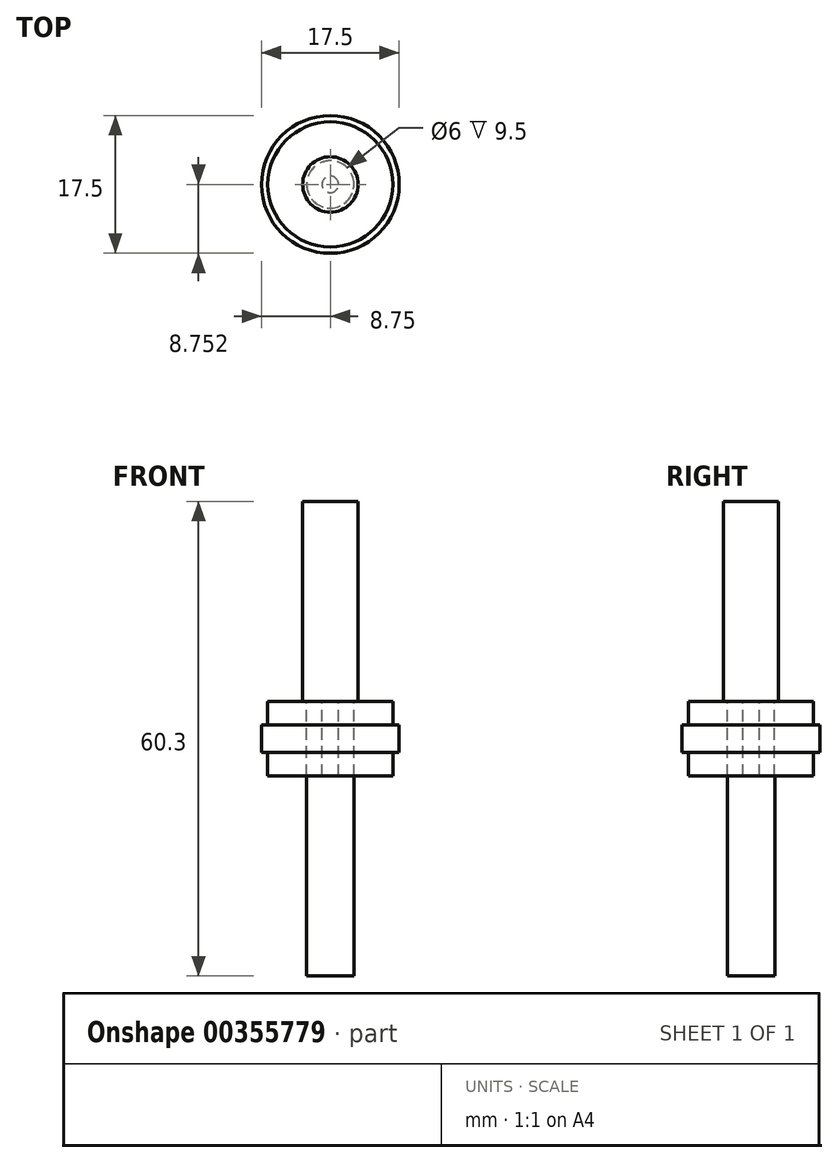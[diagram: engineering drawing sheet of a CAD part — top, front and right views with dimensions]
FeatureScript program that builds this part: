
annotation { "Feature Type Name" : "Feature", "Feature Type Description" : "" }
export const myFeature = defineFeature(function(context is Context, id is Id, definition is map)
    precondition{}
    {
        {
            var Q0;
            Q0=qCreatedBy(makeId("Top.planeOp"),FACE);
            var sketch = newSketch(context, id + "F0", { "sketchPlane" : qUnion([Q0])});
            skCircle(sketch, "E0", {"center": v(-41.02, 34.52) * mm, "radius": 7.95 * mm});
            skSolve(sketch);
        }
        {
            var Q0;
            Q0 = qSketchRegion(id + "F0", true);
            extrude(context, id + "F1", {"entities" : qUnion([Q0]), "depth" : 3 * mm});
        }
        {
            var Q0;
            Q0=makeQuery(id+"F1.opExtrude","CAP_FACE",FACE,{"disambiguationData":[OSD([sQuery(id+"F0.wireOp",EDGE,"E0")])],"isStart":false});
            var sketch = newSketch(context, id + "F2", { "sketchPlane" : qUnion([Q0])});
            skCircle(sketch, "E1", {"center": v(-41.02, 34.52) * mm, "radius": 8.75 * mm});
            skSolve(sketch);
        }
        {
            var Q0;
            Q0 = qSketchRegion(id + "F2", true);
            extrude(context, id + "F3", {"entities" : qUnion([Q0]), "operationType" : NewBodyOperationType.ADD, "depth" : 3.5 * mm});
        }
        {
            var Q0;
            Q0=makeQuery(id+"F3.opExtrude","CAP_FACE",FACE,{"disambiguationData":[OSD([sQuery(id+"F2.wireOp",EDGE,"E1")])],"isStart":false});
            var sketch = newSketch(context, id + "F4", { "sketchPlane" : qUnion([Q0])});
            skCircle(sketch, "E2", {"center": v(-41.02, 34.52) * mm, "radius": 7.95 * mm});
            skSolve(sketch);
        }
        {
            var Q0;
            Q0 = qSketchRegion(id + "F4", true);
            extrude(context, id + "F5", {"entities" : qUnion([Q0]), "operationType" : NewBodyOperationType.ADD, "depth" : 3 * mm});
        }
        {
            var Q0;
            Q0=makeQuery(id+"F5.opExtrude","CAP_FACE",FACE,{"disambiguationData":[OSD([sQuery(id+"F4.wireOp",EDGE,"E2")])],"isStart":false});
            var sketch = newSketch(context, id + "F6", { "sketchPlane" : qUnion([Q0])});
            skCircle(sketch, "E3", {"center": v(-41.02, 34.52) * mm, "radius": 3 * mm});
            skCircle(sketch, "E4", {"center": v(-41.02, 34.52) * mm, "radius": 1.05 * mm});
            skSolve(sketch);
        }
        {
            var Q0;
            Q0=makeQuery(id+"F6.imprint","IMPRINT",FACE,{"disambiguationData":[TD([[makeQuery(id+"F6.imprint","IMPRINT",EDGE,{"derivedFrom":sQuery(id+"F6.wireOp",EDGE,"E3")}),1.0]])]});
            extrude(context, id + "F7", {"entities" : qUnion([Q0]), "operationType" : NewBodyOperationType.REMOVE, "oppositeDirection" : true, "depth" : 10 * mm});
        }
        {
            var Q0;
            Q0=makeQuery(id+"F7.boolean.opBoolean","SPLIT",FACE,{"disambiguationData":[TD([makeQuery(id+"F7.opExtrude","SWEPT_FACE",FACE,{"disambiguationData":[OSD([sQuery(id+"F6.wireOp",EDGE,"E4")])]})])],"derivedFrom":makeQuery(id+"F1.opExtrude","CAP_FACE",FACE,{"disambiguationData":[OSD([sQuery(id+"F0.wireOp",EDGE,"E0")])],"isStart":true})});
            var sketch = newSketch(context, id + "F8", { "sketchPlane" : qUnion([Q0])});
            skCircle(sketch, "E5", {"center": v(-41.02, -34.52) * mm, "radius": 3.02 * mm});
            skSolve(sketch);
        }
        {
            var Q0;
            Q0 = qSketchRegion(id + "F8", true);
            extrude(context, id + "F9", {"entities" : qUnion([Q0]), "operationType" : NewBodyOperationType.ADD, "depth" : 25.4 * mm});
        }
        {
            var Q0;
            Q0=makeQuery(id+"F7.boolean.opBoolean","SPLIT",FACE,{"disambiguationData":[TD([makeQuery(id+"F7.opExtrude","SWEPT_FACE",FACE,{"disambiguationData":[OSD([sQuery(id+"F6.wireOp",EDGE,"E4")])]})])],"derivedFrom":makeQuery(id+"F5.opExtrude","CAP_FACE",FACE,{"disambiguationData":[OSD([sQuery(id+"F4.wireOp",EDGE,"E2")])],"isStart":false})});
            var sketch = newSketch(context, id + "F10", { "sketchPlane" : qUnion([Q0])});
            skCircle(sketch, "E6", {"center": v(-41.02, 34.52) * mm, "radius": 3.52 * mm});
            skSolve(sketch);
        }
        {
            var Q0;
            Q0 = qSketchRegion(id + "F10", true);
            extrude(context, id + "F11", {"entities" : qUnion([Q0]), "depth" : 25.4 * mm});
        }
    });
